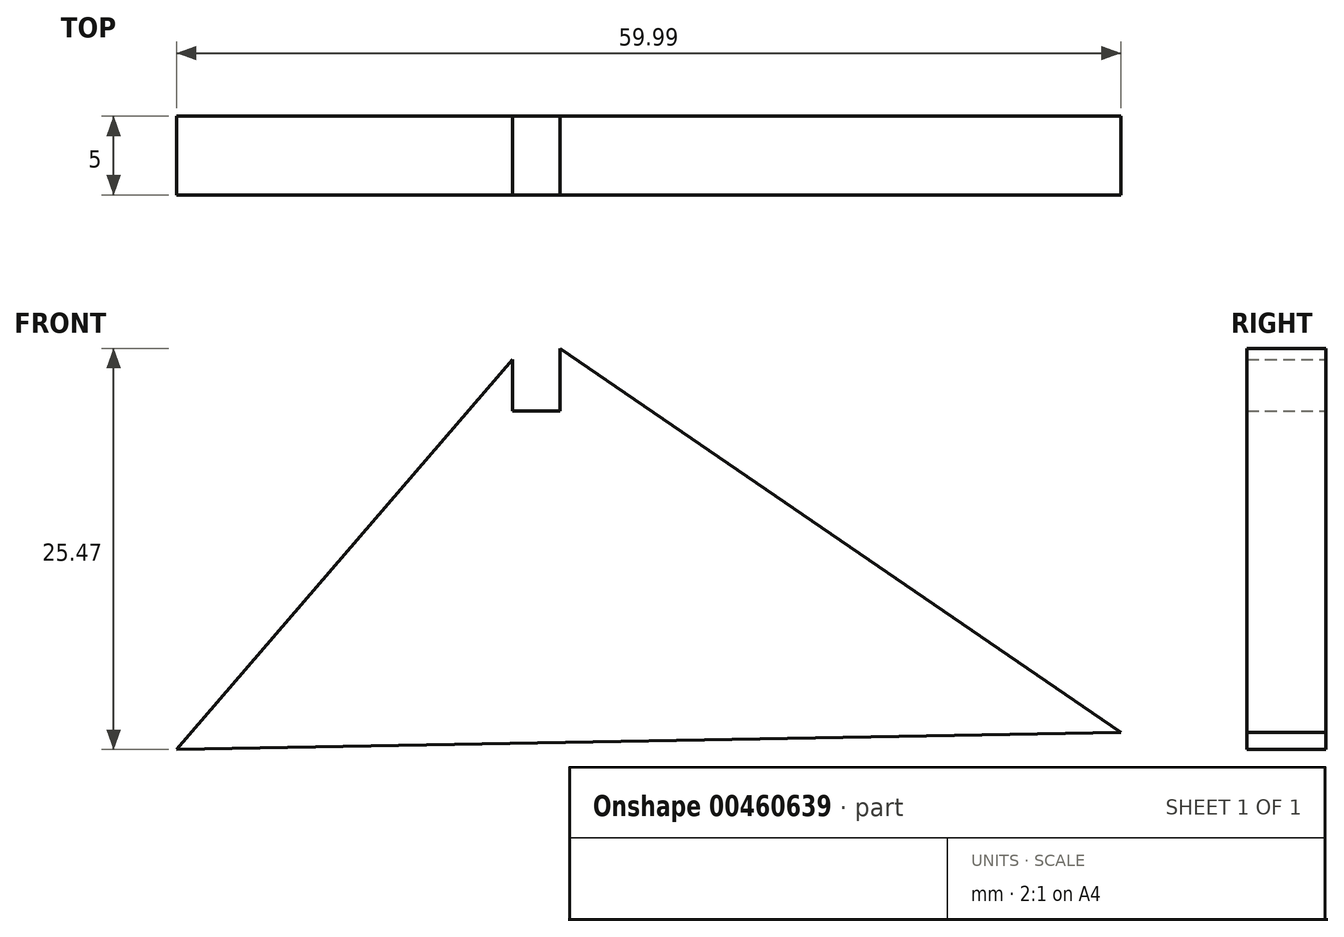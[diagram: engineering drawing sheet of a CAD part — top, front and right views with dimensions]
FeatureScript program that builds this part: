
annotation { "Feature Type Name" : "Feature", "Feature Type Description" : "" }
export const myFeature = defineFeature(function(context is Context, id is Id, definition is map)
    precondition{}
    {
        {
            var Q0;
            Q0=qCreatedBy(makeId("Front.planeOp"),FACE);
            var sketch = newSketch(context, id + "F0", { "sketchPlane" : qUnion([Q0])});
            skLineSegment(sketch, "E0", {"start": v(-33.06, 6.75) * mm, "end": v(-11.7, 31.51) * mm});
            skLineSegment(sketch, "E1", {"start": v(-8.7, 32.22) * mm, "end": v(26.93, 7.83) * mm});
            skLineSegment(sketch, "E2", {"start": v(26.93, 7.83) * mm, "end": v(-33.06, 6.75) * mm});
            skLineSegment(sketch, "E3.bottom", {"start": v(-8.7, 28.25) * mm, "end": v(-11.7, 28.25) * mm});
            skLineSegment(sketch, "E3.left", {"start": v(-8.7, 28.25) * mm, "end": v(-8.7, 32.22) * mm});
            skLineSegment(sketch, "E3.right", {"start": v(-11.7, 28.25) * mm, "end": v(-11.7, 31.51) * mm});
            skPoint(sketch, "E3.middle", {"position": v(-10.2, 33.25) * mm});
            skPoint(sketch, "E4.orphan", {"position": v(-8.7, 38.25) * mm});
            skPoint(sketch, "E5.orphan", {"position": v(-11.7, 38.25) * mm});
            skSolve(sketch);
        }
        {
            var Q0;
            Q0 = qSketchRegion(id + "F0", true);
            extrude(context, id + "F1", {"entities" : qUnion([Q0]), "depth" : 5 * mm});
        }
    });
